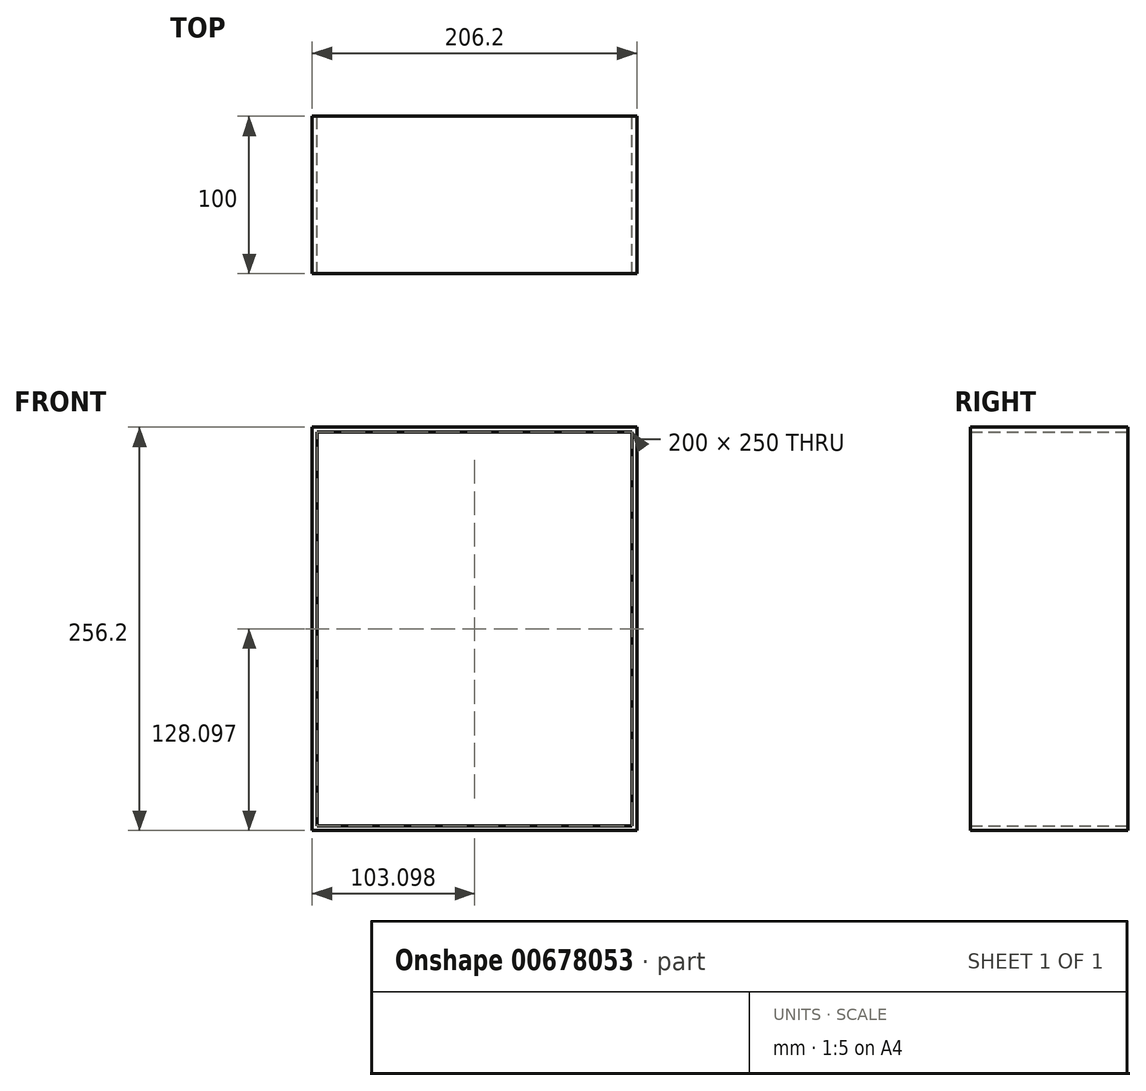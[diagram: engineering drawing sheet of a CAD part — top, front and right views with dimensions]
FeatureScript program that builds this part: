
annotation { "Feature Type Name" : "Feature", "Feature Type Description" : "" }
export const myFeature = defineFeature(function(context is Context, id is Id, definition is map)
    precondition{}
    {
        {
            var Q0;
            Q0=qCreatedBy(makeId("Front.planeOp"),FACE);
            var sketch = newSketch(context, id + "F0", { "sketchPlane" : qUnion([Q0])});
            skLineSegment(sketch, "E0.bottom", {"start": v(101.04, -67.21) * mm, "end": v(-98.96, -67.21) * mm});
            skLineSegment(sketch, "E0.top", {"start": v(101.04, 182.79) * mm, "end": v(-98.96, 182.79) * mm});
            skLineSegment(sketch, "E0.left", {"start": v(101.04, -67.21) * mm, "end": v(101.04, 182.79) * mm});
            skLineSegment(sketch, "E0.right", {"start": v(-98.96, -67.21) * mm, "end": v(-98.96, 182.79) * mm});
            skPoint(sketch, "E0.middle", {"position": v(1.04, 57.79) * mm});
            skLineSegment(sketch, "E1.bottom", {"start": v(104.14, -70.31) * mm, "end": v(-102.06, -70.31) * mm});
            skLineSegment(sketch, "E1.top", {"start": v(104.14, 185.89) * mm, "end": v(-102.06, 185.89) * mm});
            skLineSegment(sketch, "E1.left", {"start": v(104.14, -70.31) * mm, "end": v(104.14, 185.89) * mm});
            skLineSegment(sketch, "E1.right", {"start": v(-102.06, -70.31) * mm, "end": v(-102.06, 185.89) * mm});
            skSolve(sketch);
        }
        {
            var Q0;
            Q0 = qSketchRegion(id + "F0", true);
            extrude(context, id + "F1", {"entities" : qUnion([Q0]), "depth" : 100 * mm, "offsetDistance" : 25 * mm});
        }
    });
